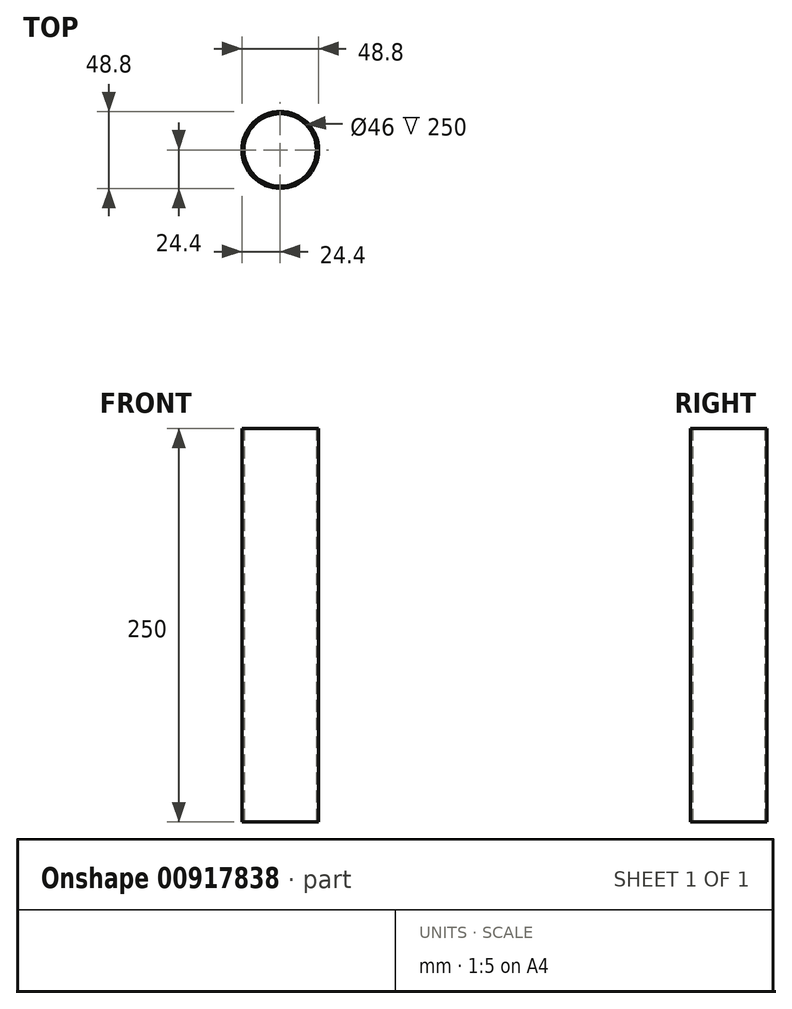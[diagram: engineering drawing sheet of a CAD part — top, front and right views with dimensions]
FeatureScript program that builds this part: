
annotation { "Feature Type Name" : "Feature", "Feature Type Description" : "" }
export const myFeature = defineFeature(function(context is Context, id is Id, definition is map)
    precondition{}
    {
        {
            var Q0;
            Q0=qCreatedBy(makeId("Top.planeOp"),FACE);
            var sketch = newSketch(context, id + "F0", { "sketchPlane" : qUnion([Q0])});
            skCircle(sketch, "E0", {"center": v(0, 0) * mm, "radius": 24.4 * mm});
            skCircle(sketch, "E1", {"center": v(0, 0) * mm, "radius": 23 * mm});
            skSolve(sketch);
        }
        {
            var Q0;
            Q0=makeQuery(id+"F0.imprint","IMPRINT",FACE,{"disambiguationData":[TD([[makeQuery(id+"F0.imprint","IMPRINT",EDGE,{"derivedFrom":sQuery(id+"F0.wireOp",EDGE,"E0")}),1.0]])]});
            extrude(context, id + "F1", {"entities" : qUnion([Q0]), "depth" : 250 * mm, "offsetDistance" : 25 * mm});
        }
    });
